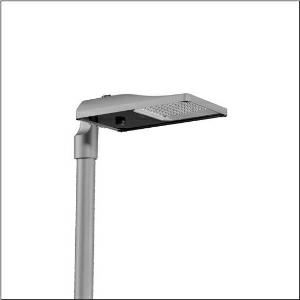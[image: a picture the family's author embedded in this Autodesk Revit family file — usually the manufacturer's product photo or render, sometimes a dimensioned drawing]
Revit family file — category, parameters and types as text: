
# Revit family: streetlight_sl_31_midi___st1_0a_5xh7d71t08qa_be0b
name_source: partatom
category: Lighting Fixtures
units: mm (PartAtom-declared; Revit-internal decimal feet)

## family parameters
Cut with Voids When Loaded = No
Host = Face
Light Source = No
Part Type = Normal
Room Calculation Point = No
Round Connector Dimension = Use Diameter
Shared = No

## types (1)
- --- (1 x LED, 19710 lm, 163.8 W, 2200K)
    Apparent Load = 164 VA
    CIE Flux Codes = 40 73 97 100 100
    Color Rendering = 70
    Color Temperature = 2200K
    Default Elevation = 1800 mm
    Description = Streetlight SL 31 midi D4i, Desk-Remote mast luminaire for post-top, side-entry; light control with lens of PMMA; light distribution: ST1.0a, direct asymmetric distribution, for standard-compliant lighting for roads and squares; LED: luminous flux: 19.710lm, light colour: 722, colour temperature: 2200K; luminous efficacy: 120,3lm/W; control: pre-setting: logarithmic dimming characteristic, flexible luminous flux parameterisation, time-dependent luminous flux control, constant luminous flux control, power reduction, intelligent temperature release in ECG and LED module, overheat protection; luminaire housing, of diecast aluminium, SITECO metallic grey (DB 702S), corrosivity category C5 high according to DIN EN ISO 12944; cover of toughened safety glass, transparent, opened without tools; mast flange of diecast aluminium, SITECO metallic grey (DB 702S), spigot size: 76/60mm, mast flange included unmounted; cable length: 14,5m, connection cable pre-assembled; mains connection: 220..240V, AC, 50/60Hz; power consumption (at start of service life): 163,8W / (at end of service life): 179W / (with reduced operation 50%): 72,6W; protection rating (complete): IP66; insulation class (complete): insulation class II (safety insulation); impact resistance: IK09; certification: CE, ENEC, ENEC+, VDE, UKCA, ZD4i; permissible operating ambient temperature for outdoor applications: -40..+50°C; packaging unit: 1 piece

Light Distribution: ST1.0a
    Height = 79 mm
    Lamp = 1 x LED
    Lamp Light Flux = 19710 lm
    Lamp Power = 163.8 W
    Lamp count = 1
    Length = 577 mm
    Luminous efficacy = 120 lm/W
    Manufacturer = Siteco
    ModVariant = No
    Model = 5XH7D71T08QA
    Number of Poles = 1
    OnlyDefault = Yes
    Power Factor = 1
    Product Name = Streetlight SL 31 midi | ST1.0a
    Product group = mast luminaire | pylon top
    ProductGroupID = 6100
    Protection Class = Protection class II
    Protection Degree = IP 66
    RLX_Detail_Level = 1
    RLX_Emergency_Light_Flux = 0 lm
    RLX_Emergency_Type = 0
    RLX_Emergency_Type_DB = No
    RlxData = <blob elided: 26485 chars, md5=eb3eaaa1>
    Socket = socket
    Standby Power = 0 W
    System Light Flux = 19710 lm
    System Power = 164 W
    Type Comments = factory setting: luminous flux: 100 % | dim-lin: 254 | 865 mA
    Type Image = l_1300321.jpg
    URL = http://relux.com
    VarID = @adj_009123
    Voltage = 0 V
    Weight = 0.00 kg
    Width = 362 mm

## geometry (parser evidence)
native form markers: Blend x4, Sweep x12
no freeform markers — native parametric forms only
